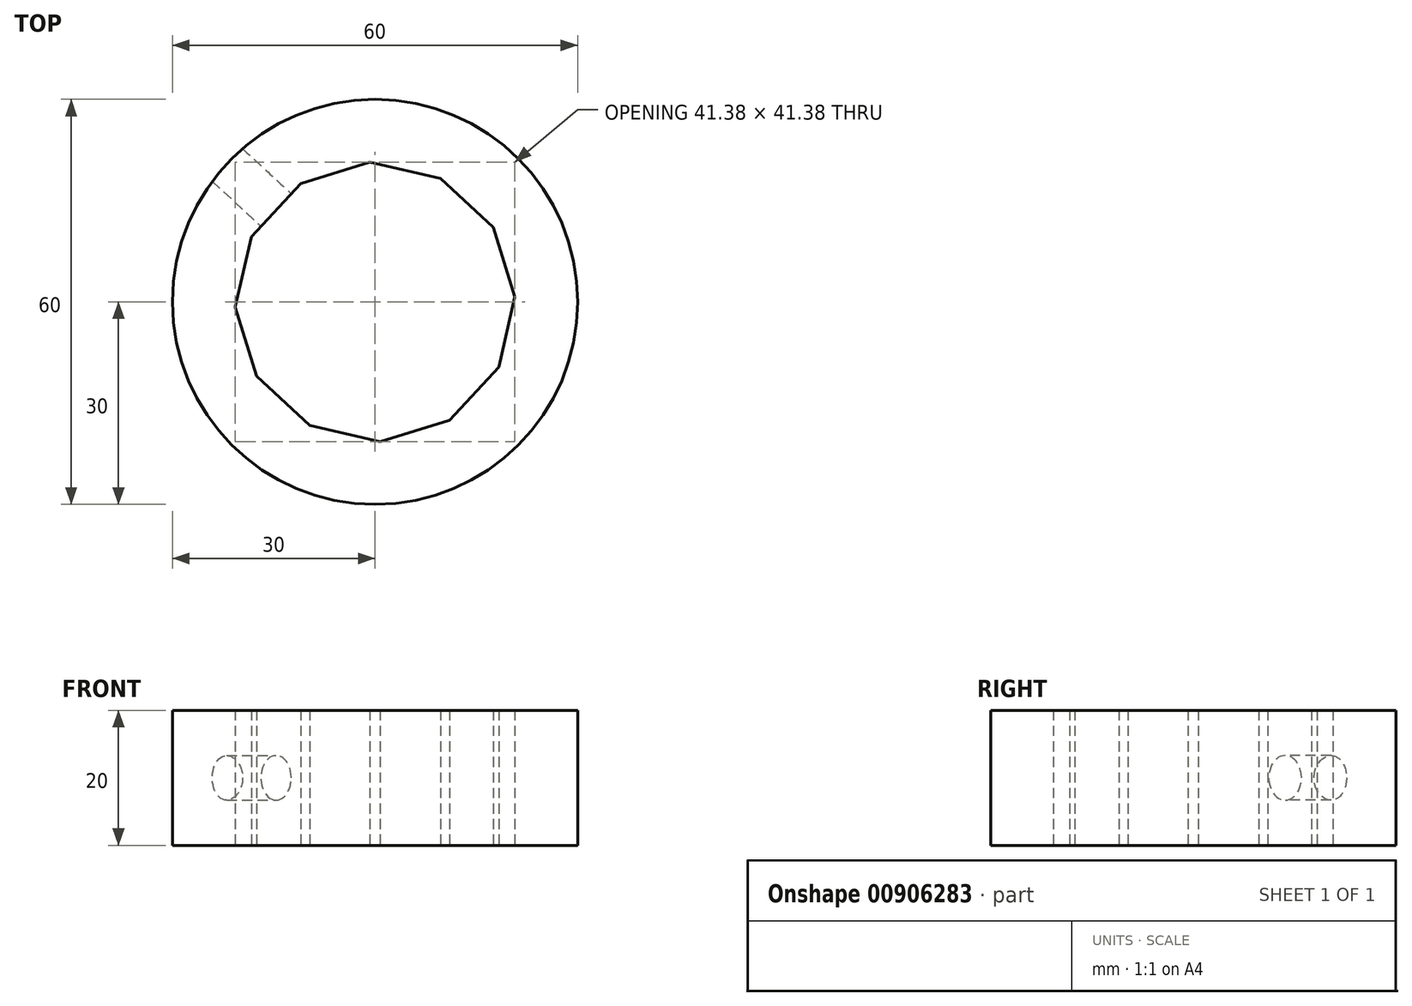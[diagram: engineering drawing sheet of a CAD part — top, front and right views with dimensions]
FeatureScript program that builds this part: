
annotation { "Feature Type Name" : "Feature", "Feature Type Description" : "" }
export const myFeature = defineFeature(function(context is Context, id is Id, definition is map)
    precondition{}
    {
        {
            var Q0;
            Q0=qCreatedBy(makeId("Top.planeOp"),FACE);
            var sketch = newSketch(context, id + "F0", { "sketchPlane" : qUnion([Q0])});
            skCircle(sketch, "E0", {"center": v(0, 0) * mm, "radius": 30 * mm});
            skCircle(sketch, "E1", {"center": v(0, 0) * mm, "radius": 10 * mm});
            skCircle(sketch, "E2", {"center": v(0, 0) * mm, "radius": 20 * mm});
            skCircle(sketch, "E3.cCircle", {"center": v(0, 0) * mm, "radius": 20 * mm, "construction": true});
            skLineSegment(sketch, "E3.0", {"start": v(-0.77, 20.7) * mm, "end": v(9.68, 18.3) * mm});
            skLineSegment(sketch, "E3.1", {"start": v(9.68, 18.3) * mm, "end": v(17.53, 11.02) * mm});
            skLineSegment(sketch, "E3.2", {"start": v(17.53, 11.02) * mm, "end": v(20.7, 0.77) * mm});
            skLineSegment(sketch, "E3.3", {"start": v(20.7, 0.77) * mm, "end": v(18.3, -9.68) * mm});
            skLineSegment(sketch, "E3.4", {"start": v(18.3, -9.68) * mm, "end": v(11.02, -17.53) * mm});
            skLineSegment(sketch, "E3.5", {"start": v(11.02, -17.53) * mm, "end": v(0.77, -20.7) * mm});
            skLineSegment(sketch, "E3.6", {"start": v(0.77, -20.7) * mm, "end": v(-9.68, -18.3) * mm});
            skLineSegment(sketch, "E3.7", {"start": v(-9.68, -18.3) * mm, "end": v(-17.53, -11.02) * mm});
            skLineSegment(sketch, "E3.8", {"start": v(-17.53, -11.02) * mm, "end": v(-20.7, -0.77) * mm});
            skLineSegment(sketch, "E3.9", {"start": v(-20.7, -0.77) * mm, "end": v(-18.3, 9.68) * mm});
            skLineSegment(sketch, "E3.10", {"start": v(-18.3, 9.68) * mm, "end": v(-11.02, 17.53) * mm});
            skLineSegment(sketch, "E3.11", {"start": v(-11.02, 17.53) * mm, "end": v(-0.77, 20.7) * mm});
            skPoint(sketch, "E3.0.midPoint", {"position": v(4.45, 19.5) * mm});
            skSolve(sketch);
        }
        {
            var Q0;
            Q0=makeQuery(id+"F0.imprint","IMPRINT",FACE,{"disambiguationData":[TD([[makeQuery(id+"F0.imprint","IMPRINT",EDGE,{"derivedFrom":sQuery(id+"F0.wireOp",EDGE,"E0")}),1.0]])]});
            extrude(context, id + "F1", {"entities" : qUnion([Q0]), "depth" : 20 * mm, "offsetDistance" : 25 * mm});
        }
        {
            var Q0;
            Q0=makeQuery(id+"F1.opExtrude","SWEPT_FACE",FACE,{"disambiguationData":[OSD([sQuery(id+"F0.wireOp",EDGE,"E3.10")])]});
            var sketch = newSketch(context, id + "F2", { "sketchPlane" : qUnion([Q0])});
            skPoint(sketch, "E4", {"position": v(0, 10) * mm});
            skPoint(sketch, "E4.positionSnap0", {"position": v(-5.36, 10) * mm});
            skSolve(sketch);
        }
        {
            var Q0;
            Q0=sQuery(id+"F2.wireOp",VERTEX,"E4");
            var Q1;
            Q1=makeQuery(id+"F1.opExtrude","SWEPT_BODY",BODY,{"disambiguationData":[OSD([sQuery(id+"F0.wireOp",EDGE,"E0"),sQuery(id+"F0.wireOp",EDGE,"E3.0"),sQuery(id+"F0.wireOp",EDGE,"E3.1"),sQuery(id+"F0.wireOp",EDGE,"E3.2"),sQuery(id+"F0.wireOp",EDGE,"E3.3"),sQuery(id+"F0.wireOp",EDGE,"E3.4"),sQuery(id+"F0.wireOp",EDGE,"E3.5"),sQuery(id+"F0.wireOp",EDGE,"E3.6"),sQuery(id+"F0.wireOp",EDGE,"E3.7"),sQuery(id+"F0.wireOp",EDGE,"E3.8"),sQuery(id+"F0.wireOp",EDGE,"E3.9"),sQuery(id+"F0.wireOp",EDGE,"E3.10"),sQuery(id+"F0.wireOp",EDGE,"E3.11")])]});
            hole(context, id + "F3", {"style" : HoleStyle.SIMPLE, "endStyle" : HoleEndStyle.BLIND, "standardTappedOrClearance" : lookupTablePath({ "fit" : "Normal", "standard" : "ISO", "size" : "M6", "type" : "Clearance" }), "standardBlindInLast" : lookupTablePath({ "fit" : "Normal", "standard" : "ISO", "size" : "M6", "type" : "Clearance" }), "holeDiameter" : 6.6 * mm, "majorDiameter" : 5 * mm, "holeDepth" : 20 * mm, "isTappedThrough" : true, "tappedDepth" : 12 * mm, "tapClearance" : 3, "locations" : qUnion([Q0]), "scope" : qUnion([Q1])});
        }
    });
